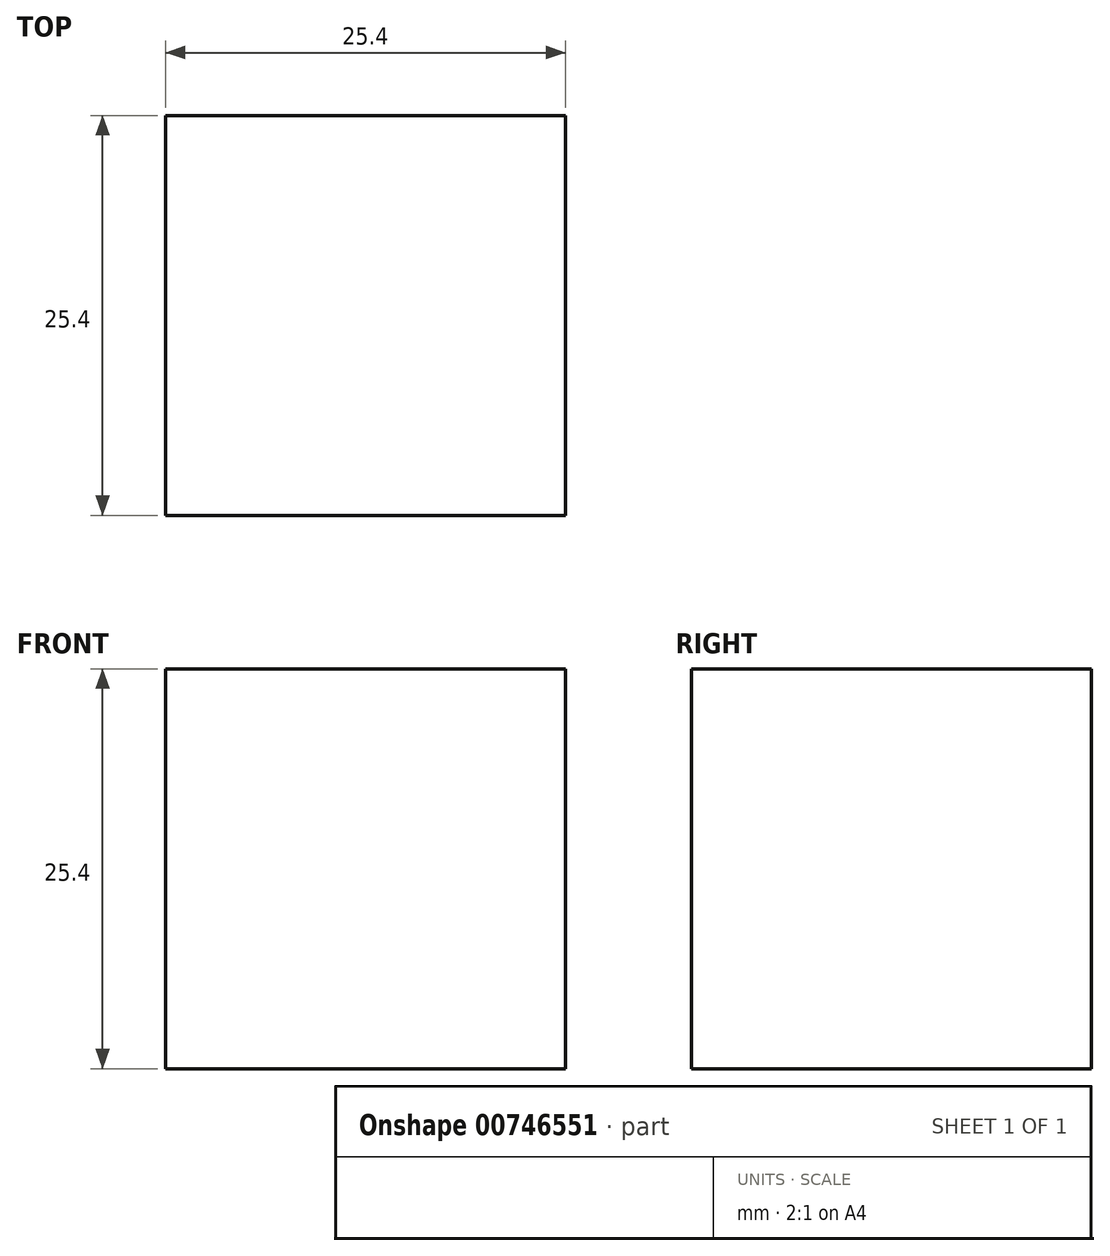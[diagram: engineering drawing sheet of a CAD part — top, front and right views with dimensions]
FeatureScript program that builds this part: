
annotation { "Feature Type Name" : "Feature", "Feature Type Description" : "" }
export const myFeature = defineFeature(function(context is Context, id is Id, definition is map)
    precondition{}
    {
        {
            var Q0;
            Q0=qCreatedBy(makeId("Top.planeOp"),FACE);
            var sketch = newSketch(context, id + "F0", { "sketchPlane" : qUnion([Q0])});
            skLineSegment(sketch, "E0.bottom", {"start": v(32.59, 42.03) * mm, "end": v(7.19, 42.03) * mm});
            skLineSegment(sketch, "E0.top", {"start": v(32.59, 16.63) * mm, "end": v(7.19, 16.63) * mm});
            skLineSegment(sketch, "E0.left", {"start": v(32.59, 42.03) * mm, "end": v(32.59, 16.63) * mm});
            skLineSegment(sketch, "E0.right", {"start": v(7.19, 42.03) * mm, "end": v(7.19, 16.63) * mm});
            skSolve(sketch);
        }
        {
            var Q0;
            Q0=makeQuery(id+"F0.imprint","IMPRINT",FACE,{"disambiguationData":[TD([[makeQuery(id+"F0.imprint","IMPRINT",EDGE,{"derivedFrom":sQuery(id+"F0.wireOp",EDGE,"E0.bottom")}),1.0]])]});
            extrude(context, id + "F1", {"entities" : qUnion([Q0]), "depth" : 25.4 * mm, "offsetDistance" : 25.4 * mm});
        }
    });
